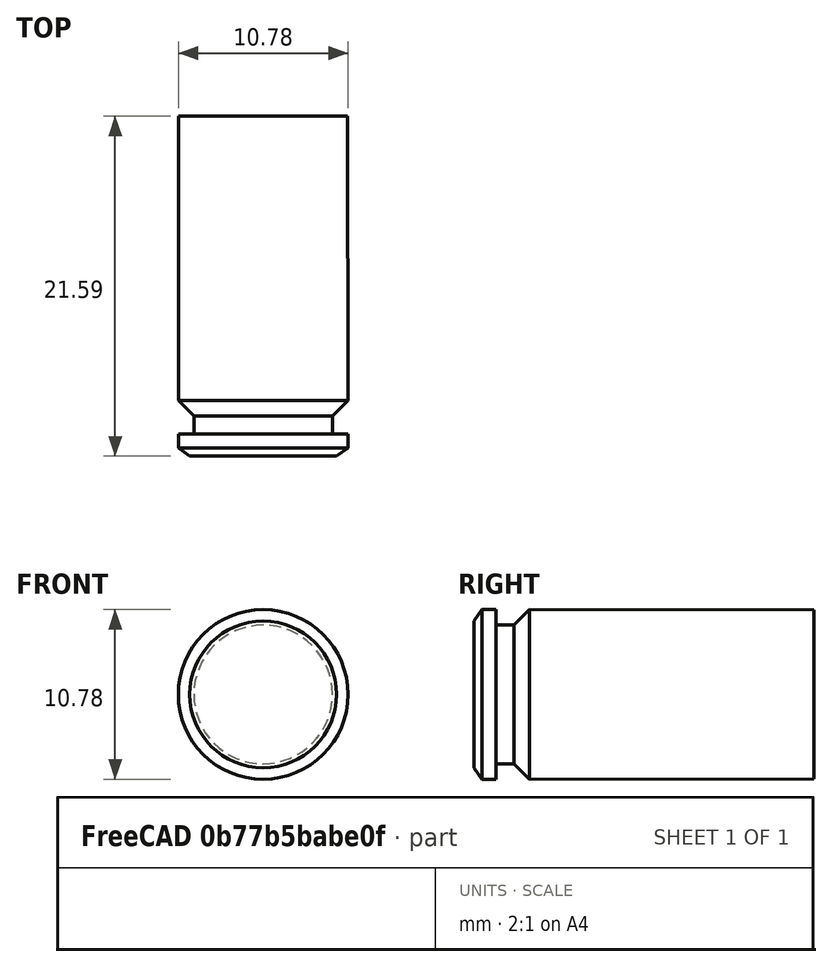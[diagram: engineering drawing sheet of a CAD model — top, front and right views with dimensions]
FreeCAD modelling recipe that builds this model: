
FCSTD DOCUMENT
Label: 40SW
objects: Sketcher::SketchObject×1, PartDesign::Revolution×1
note: 2 computed .brp shape members not serialized (recipe doc carries the construction recipe); baked Part::Feature solids carry a one-line shape summary decoded from their .brp

FEATURE [Sketcher::SketchObject] Sketch
  sketch-geometry (9):
    g0: LineSegment StartX=0 StartY=0 StartZ=0 EndX=4.66164 EndY=0 EndZ=0
    g1: LineSegment StartX=4.66164 StartY=0 StartZ=0 EndX=5.39 EndY=0.51 EndZ=0
    g2: LineSegment StartX=5.39 StartY=0.51 StartZ=0 EndX=5.39 EndY=1.4 EndZ=0
    g3: LineSegment StartX=5.39 StartY=1.4 StartZ=0 EndX=4.4 EndY=1.4 EndZ=0
    g4: LineSegment StartX=4.4 StartY=1.4 StartZ=0 EndX=4.4 EndY=2.54 EndZ=0
    g5: LineSegment StartX=4.4 StartY=2.54 StartZ=0 EndX=5.39 EndY=3.52 EndZ=0
    g6: LineSegment StartX=5.39 StartY=3.52 StartZ=0 EndX=5.37 EndY=21.59 EndZ=0
    g7: LineSegment StartX=5.37 StartY=21.59 StartZ=0 EndX=0 EndY=21.59 EndZ=0
    g8: LineSegment StartX=0 StartY=21.59 StartZ=0 EndX=0 EndY=0 EndZ=0
  constraints (27):
    c: Coincident(g0,g1)
    c: Coincident(g1,g2)
    c: Coincident(g2,g3)
    c: Horizontal(g3)
    c: Coincident(g3,g4)
    c: Vertical(g4)
    c: Coincident(g4,g5)
    c: Coincident(g5,g6)
    c: Coincident(g6,g7)
    c: Horizontal(g7)
    c: Coincident(g7,g8)
    c: Vertical(g8)
    c: Coincident(g0,g8)
    c: Vertical(g2)
    c: DistanceY(g1,g0) = -0.51
    c: DistanceY(g2,g0) = -1.4
    c: DistanceY(g4,g3) = -1.14
    c: DistanceY(g0,g6) = 21.59
    c: Horizontal(g0)
    c: DistanceY(g5,g0) = -3.52
    c: DistanceX(g7) = -5.37
    c: DistanceX(g5,g0) = -5.39
    c: DistanceX(g3,g0) = -4.4
    c: DistanceX(g1,g0) = -5.39
    c: Angle(g1) = 0.610865
    c: DistanceX(g0) = 0
    c: DistanceY(g0) = 0
FEATURE [PartDesign::Revolution] Revolution
  Angle = 360
  Axis = (0,1,0)
  Base = (0,0,0)
  Sketch = -> Sketch
